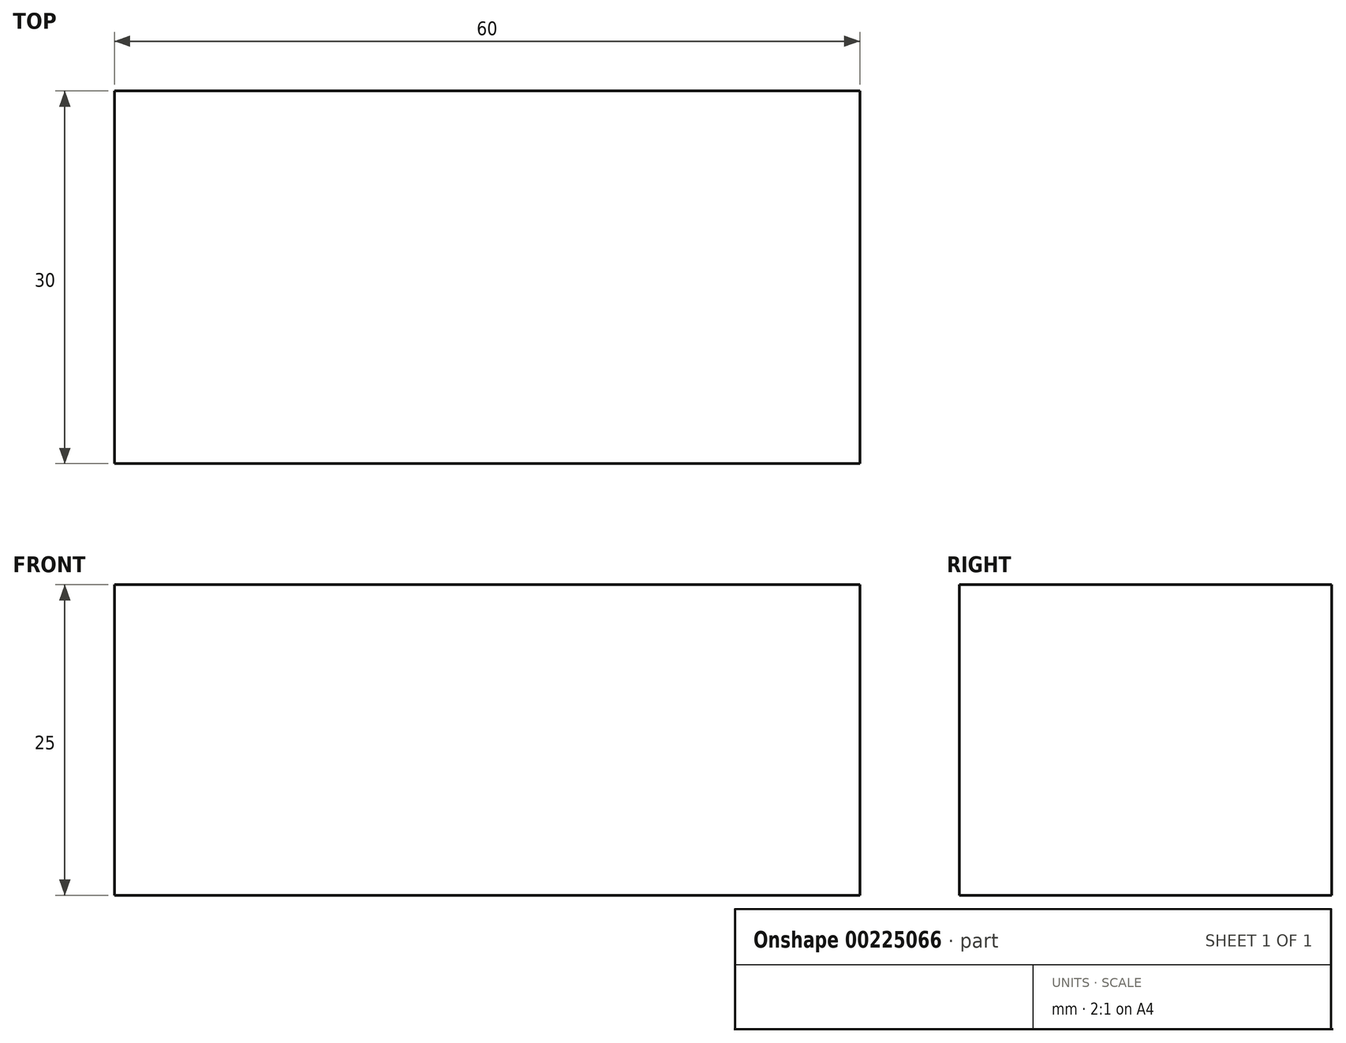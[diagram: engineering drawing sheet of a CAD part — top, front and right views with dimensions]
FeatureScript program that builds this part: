
annotation { "Feature Type Name" : "Feature", "Feature Type Description" : "" }
export const myFeature = defineFeature(function(context is Context, id is Id, definition is map)
    precondition{}
    {
        {
            var Q0;
            Q0=qCreatedBy(makeId("Front.planeOp"),FACE);
            var sketch = newSketch(context, id + "F0", { "sketchPlane" : qUnion([Q0])});
            skLineSegment(sketch, "E0.bottom", {"start": v(0, 0) * mm, "end": v(60, 0) * mm});
            skLineSegment(sketch, "E0.top", {"start": v(0, 25) * mm, "end": v(60, 25) * mm});
            skLineSegment(sketch, "E0.left", {"start": v(0, 0) * mm, "end": v(0, 25) * mm});
            skLineSegment(sketch, "E0.right", {"start": v(60, 0) * mm, "end": v(60, 25) * mm});
            skSolve(sketch);
        }
        {
            var Q0;
            Q0=makeQuery(id+"F0.imprint","IMPRINT",FACE,{"disambiguationData":[TD([[makeQuery(id+"F0.imprint","IMPRINT",EDGE,{"derivedFrom":sQuery(id+"F0.wireOp",EDGE,"E0.bottom")}),1.0]])]});
            extrude(context, id + "F1", {"entities" : qUnion([Q0]), "endBound" : BoundingType.SYMMETRIC, "depth" : 30 * mm});
        }
    });
